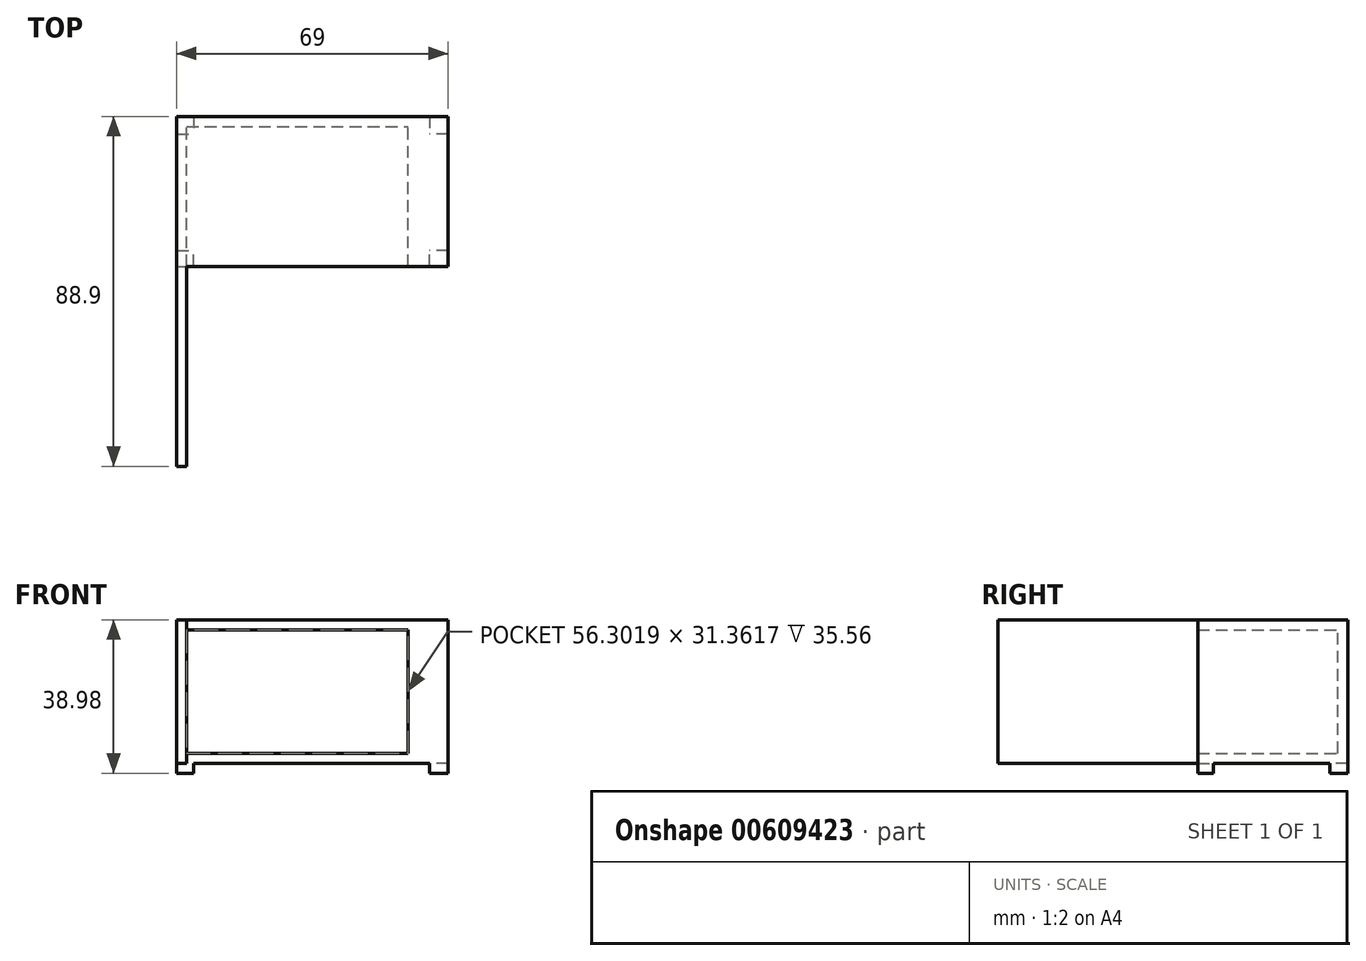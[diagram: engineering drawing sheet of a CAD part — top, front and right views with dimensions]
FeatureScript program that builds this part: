
annotation { "Feature Type Name" : "Feature", "Feature Type Description" : "" }
export const myFeature = defineFeature(function(context is Context, id is Id, definition is map)
    precondition{}
    {
        {
            var Q0;
            Q0=qCreatedBy(makeId("Front.planeOp"),FACE);
            var sketch = newSketch(context, id + "F0", { "sketchPlane" : qUnion([Q0])});
            skLineSegment(sketch, "E0.bottom", {"start": v(0, 0) * mm, "end": v(61.38, 0) * mm});
            skLineSegment(sketch, "E0.top", {"start": v(0, 36.44) * mm, "end": v(61.38, 36.44) * mm});
            skLineSegment(sketch, "E0.left", {"start": v(0, 0) * mm, "end": v(0, 36.44) * mm});
            skLineSegment(sketch, "E0.right", {"start": v(61.38, 0) * mm, "end": v(61.38, 36.44) * mm});
            skSolve(sketch);
        }
        {
            var Q0;
            Q0 = qSketchRegion(id + "F0", true);
            extrude(context, id + "F1", {"entities" : qUnion([Q0]), "depth" : 38.1 * mm, "offsetDistance" : 25.4 * mm});
        }
        {
            var Q0;
            Q0=makeQuery(id+"F1.opExtrude","CAP_FACE",FACE,{"disambiguationData":[OSD([sQuery(id+"F0.wireOp",EDGE,"E0.bottom"),sQuery(id+"F0.wireOp",EDGE,"E0.top"),sQuery(id+"F0.wireOp",EDGE,"E0.left"),sQuery(id+"F0.wireOp",EDGE,"E0.right")])],"isStart":false});
            shell(context, id + "F2", {"entities" : qUnion([Q0]), "thickness" : 2.54 * mm});
        }
        {
            var Q0;
            Q0=makeQuery(id+"F1.opExtrude","SWEPT_FACE",FACE,{"disambiguationData":[OSD([sQuery(id+"F0.wireOp",EDGE,"E0.right")])]});
            extrude(context, id + "F3", {"entities" : qUnion([Q0]), "operationType" : NewBodyOperationType.ADD, "depth" : 7.62 * mm, "offsetDistance" : 25.4 * mm});
        }
        {
            var Q0;
            {var subQ0=sQuery(id+"F0.wireOp",EDGE,"E0.right");Q0=makeQuery(id+"F3.boolean.opBoolean","MERGE",FACE,{"derivedFrom":[makeQuery(id+"F1.opExtrude","CAP_FACE",FACE,{"disambiguationData":[OSD([sQuery(id+"F0.wireOp",EDGE,"E0.bottom"),sQuery(id+"F0.wireOp",EDGE,"E0.top"),sQuery(id+"F0.wireOp",EDGE,"E0.left"),subQ0])],"isStart":false}),makeQuery(id+"F3.opExtrude","SWEPT_FACE",FACE,{"disambiguationData":[OSD([subQ0]),TDD([makeQuery(id+"F1.opExtrude","CAP_EDGE",EDGE,{"disambiguationData":[OSD([subQ0])],"isStart":false})])]})]});}
            var sketch = newSketch(context, id + "F4", { "sketchPlane" : qUnion([Q0])});
            skLineSegment(sketch, "E1.bottom", {"start": v(0, 0) * mm, "end": v(2.54, 0) * mm});
            skLineSegment(sketch, "E1.top", {"start": v(0, 36.44) * mm, "end": v(2.54, 36.44) * mm});
            skLineSegment(sketch, "E1.left", {"start": v(0, 0) * mm, "end": v(0, 36.44) * mm});
            skLineSegment(sketch, "E1.right", {"start": v(2.54, 0) * mm, "end": v(2.54, 36.44) * mm});
            skSolve(sketch);
        }
        {
            var Q0;
            Q0 = qSketchRegion(id + "F4", true);
            extrude(context, id + "F5", {"entities" : qUnion([Q0]), "operationType" : NewBodyOperationType.ADD, "depth" : 50.8 * mm, "offsetDistance" : 25.4 * mm});
        }
        {
            var Q0;
            {var subQ0=sQuery(id+"F0.wireOp",EDGE,"E0.bottom");Q0=makeQuery(id+"F5.boolean.opBoolean","MERGE",FACE,{"derivedFrom":[makeQuery(id+"F3.boolean.opBoolean","MERGE",FACE,{"derivedFrom":[makeQuery(id+"F1.opExtrude","SWEPT_FACE",FACE,{"disambiguationData":[OSD([subQ0])]}),makeQuery(id+"F3.opExtrude","SWEPT_FACE",FACE,{"disambiguationData":[OSD([subQ0,sQuery(id+"F0.wireOp",EDGE,"E0.right")])]})]}),makeQuery(id+"F5.opExtrude","SWEPT_FACE",FACE,{"disambiguationData":[OSD([sQuery(id+"F4.wireOp",EDGE,"E1.bottom")])]})]});}
            var sketch = newSketch(context, id + "F6", { "sketchPlane" : qUnion([Q0])});
            skLineSegment(sketch, "E2", {"start": v(2.54, 38.1) * mm, "end": v(0, 38.1) * mm});
            skLineSegment(sketch, "E3.bottom", {"start": v(0, 38.1) * mm, "end": v(4.32, 38.1) * mm});
            skLineSegment(sketch, "E3.top", {"start": v(0, 34.05) * mm, "end": v(4.32, 34.05) * mm});
            skLineSegment(sketch, "E3.left", {"start": v(0, 38.1) * mm, "end": v(0, 34.05) * mm});
            skLineSegment(sketch, "E3.right", {"start": v(4.32, 38.1) * mm, "end": v(4.32, 34.05) * mm});
            skLineSegment(sketch, "E4.bottom", {"start": v(69, 38.1) * mm, "end": v(64.3, 38.1) * mm});
            skLineSegment(sketch, "E4.top", {"start": v(69, 34.05) * mm, "end": v(64.3, 34.05) * mm});
            skLineSegment(sketch, "E4.left", {"start": v(69, 38.1) * mm, "end": v(69, 34.05) * mm});
            skLineSegment(sketch, "E4.right", {"start": v(64.3, 38.1) * mm, "end": v(64.3, 34.05) * mm});
            skLineSegment(sketch, "E5.bottom", {"start": v(69, 0) * mm, "end": v(64.3, 0) * mm});
            skLineSegment(sketch, "E5.top", {"start": v(69, 4.46) * mm, "end": v(64.3, 4.46) * mm});
            skLineSegment(sketch, "E5.left", {"start": v(69, 0) * mm, "end": v(69, 4.46) * mm});
            skLineSegment(sketch, "E5.right", {"start": v(64.3, 0) * mm, "end": v(64.3, 4.46) * mm});
            skLineSegment(sketch, "E6.bottom", {"start": v(0, 0) * mm, "end": v(4.32, 0) * mm});
            skLineSegment(sketch, "E6.top", {"start": v(0, 4.46) * mm, "end": v(4.32, 4.46) * mm});
            skLineSegment(sketch, "E6.left", {"start": v(0, 0) * mm, "end": v(0, 4.46) * mm});
            skLineSegment(sketch, "E6.right", {"start": v(4.32, 0) * mm, "end": v(4.32, 4.46) * mm});
            skSolve(sketch);
        }
        {
            var Q0;
            Q0 = qSketchRegion(id + "F6", true);
            extrude(context, id + "F7", {"entities" : qUnion([Q0]), "operationType" : NewBodyOperationType.ADD, "depth" : 2.54 * mm, "offsetDistance" : 25.4 * mm});
        }
    });
